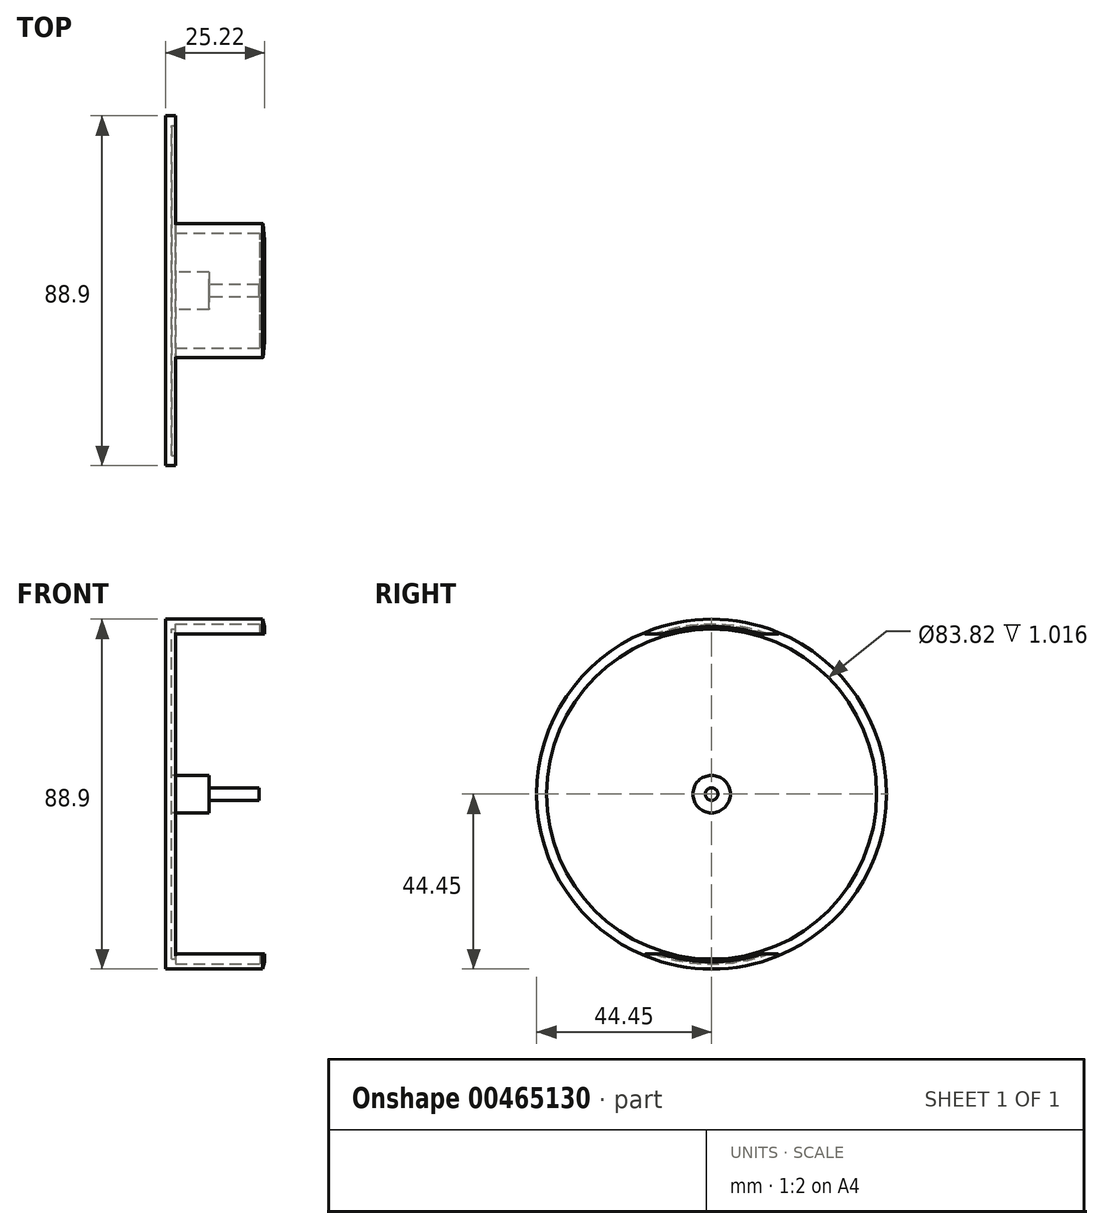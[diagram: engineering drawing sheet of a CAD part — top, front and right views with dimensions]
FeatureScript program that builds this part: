
annotation { "Feature Type Name" : "Feature", "Feature Type Description" : "" }
export const myFeature = defineFeature(function(context is Context, id is Id, definition is map)
    precondition{}
    {
        {
            var Q0;
            Q0=qCreatedBy(makeId("Right.planeOp"),FACE);
            var sketch = newSketch(context, id + "F0", { "sketchPlane" : qUnion([Q0])});
            skCircle(sketch, "E0", {"center": v(0, 0) * mm, "radius": 44.45 * mm});
            skSolve(sketch);
        }
        {
            var Q0;
            Q0 = qSketchRegion(id + "F0", true);
            extrude(context, id + "F1", {"entities" : qUnion([Q0]), "depth" : 25.4 * mm});
        }
        {
            var Q0;
            Q0=makeQuery(id+"F1.opExtrude","CAP_FACE",FACE,{"disambiguationData":[OSD([sQuery(id+"F0.wireOp",EDGE,"E0")])],"isStart":false});
            var sketch = newSketch(context, id + "F2", { "sketchPlane" : qUnion([Q0])});
            skCircle(sketch, "E1", {"center": v(0, 0) * mm, "radius": 43.18 * mm});
            skSolve(sketch);
        }
        {
            var Q0;
            Q0 = qSketchRegion(id + "F2", true);
            extrude(context, id + "F3", {"entities" : qUnion([Q0]), "operationType" : NewBodyOperationType.REMOVE, "oppositeDirection" : true, "depth" : 22.86 * mm});
        }
        {
            var Q0;
            Q0=makeQuery(id+"F1.opExtrude","CAP_FACE",FACE,{"disambiguationData":[OSD([sQuery(id+"F0.wireOp",EDGE,"E0")])],"isStart":false});
            var sketch = newSketch(context, id + "F4", { "sketchPlane" : qUnion([Q0])});
            skCircle(sketch, "E2", {"center": v(0, 0) * mm, "radius": 44.45 * mm});
            skCircle(sketch, "E3", {"center": v(0, 0) * mm, "radius": 42.55 * mm});
            skSolve(sketch);
        }
        {
            var Q0;
            Q0 = qSketchRegion(id + "F4", true);
            extrude(context, id + "F5", {"entities" : qUnion([Q0]), "operationType" : NewBodyOperationType.ADD, "oppositeDirection" : true, "depth" : 1.27 * mm});
        }
        {
            var Q0;
            Q0=qCreatedBy(makeId("Front.planeOp"),FACE);
            var sketch = newSketch(context, id + "F6", { "sketchPlane" : qUnion([Q0])});
            skLineSegment(sketch, "E4.bottom", {"start": v(27.94, 40.64) * mm, "end": v(2.54, 40.64) * mm});
            skLineSegment(sketch, "E4.top", {"start": v(27.94, -40.64) * mm, "end": v(2.54, -40.64) * mm});
            skLineSegment(sketch, "E4.left", {"start": v(27.94, 40.64) * mm, "end": v(27.94, -40.64) * mm});
            skLineSegment(sketch, "E4.right", {"start": v(2.54, 40.64) * mm, "end": v(2.54, -40.64) * mm});
            skLineSegment(sketch, "E5", {"start": v(0, 0) * mm, "end": v(2.54, 0) * mm, "construction": true});
            skSolve(sketch);
        }
        {
            var Q0;
            Q0 = qSketchRegion(id + "F6", true);
            extrude(context, id + "F7", {"entities" : qUnion([Q0]), "operationType" : NewBodyOperationType.REMOVE, "oppositeDirection" : true, "depth" : 127 * mm, "symmetric" : true});
        }
        {
            var Q0;
            {var subQ0=sQuery(id+"F4.wireOp",EDGE,"E3");Q0=makeQuery(id+"F7.boolean.opBoolean","SPLIT",EDGE,{"disambiguationData":[TD([makeQuery(id+"F7.opExtrude","SWEPT_FACE",FACE,{"disambiguationData":[OSD([sQuery(id+"F6.wireOp",EDGE,"E4.top")])]})])],"derivedFrom":makeQuery(id+"F5.opExtrude","CAP_EDGE",EDGE,{"disambiguationData":[OSD([subQ0])],"isStart":false})});}
            var Q1;
            {var subQ0=sQuery(id+"F4.wireOp",EDGE,"E3");Q1=makeQuery(id+"F7.boolean.opBoolean","SPLIT",EDGE,{"disambiguationData":[TD([makeQuery(id+"F7.opExtrude","SWEPT_FACE",FACE,{"disambiguationData":[OSD([sQuery(id+"F6.wireOp",EDGE,"E4.bottom")])]})])],"derivedFrom":makeQuery(id+"F5.opExtrude","CAP_EDGE",EDGE,{"disambiguationData":[OSD([subQ0])],"isStart":false})});}
            chamfer(context, id + "F8", {"entities" : qUnion([Q0, Q1]), "chamferType" : ChamferType.OFFSET_ANGLE, "width" : 1.27 * mm, "oppositeDirection" : true, "angle" : 15 * degree, "tangentPropagation" : true});
        }
        {
            var Q0;
            {var subQ0=sQuery(id+"F0.wireOp",EDGE,"E0");Q0=makeQuery(id+"F7.boolean.opBoolean","SPLIT",EDGE,{"disambiguationData":[TD([makeQuery(id+"F7.opExtrude","SWEPT_FACE",FACE,{"disambiguationData":[OSD([sQuery(id+"F6.wireOp",EDGE,"E4.top")])]})])],"derivedFrom":makeQuery(id+"F1.opExtrude","CAP_EDGE",EDGE,{"disambiguationData":[OSD([subQ0])],"isStart":false})});}
            var Q1;
            {var subQ0=sQuery(id+"F0.wireOp",EDGE,"E0");Q1=makeQuery(id+"F7.boolean.opBoolean","SPLIT",EDGE,{"disambiguationData":[TD([makeQuery(id+"F7.opExtrude","SWEPT_FACE",FACE,{"disambiguationData":[OSD([sQuery(id+"F6.wireOp",EDGE,"E4.bottom")])]})])],"derivedFrom":makeQuery(id+"F1.opExtrude","CAP_EDGE",EDGE,{"disambiguationData":[OSD([subQ0])],"isStart":false})});}
            chamfer(context, id + "F9", {"entities" : qUnion([Q0, Q1]), "chamferType" : ChamferType.OFFSET_ANGLE, "width" : 2.54 * mm, "oppositeDirection" : true, "angle" : 15 * degree, "tangentPropagation" : true});
        }
        {
            var Q0;
            Q0=makeQuery(id+"F7.boolean.opBoolean","INTERSECT",EDGE,{"disambiguationData":[OD(0.0)],"derivedFrom":[makeQuery(id+"F1.opExtrude","SWEPT_FACE",FACE,{"disambiguationData":[OSD([sQuery(id+"F0.wireOp",EDGE,"E0")])]}),makeQuery(id+"F7.opExtrude","SWEPT_FACE",FACE,{"disambiguationData":[OSD([sQuery(id+"F6.wireOp",EDGE,"E4.top")])]})]});
            var Q1;
            Q1=makeQuery(id+"F7.boolean.opBoolean","INTERSECT",EDGE,{"disambiguationData":[OD(1.0)],"derivedFrom":[makeQuery(id+"F1.opExtrude","SWEPT_FACE",FACE,{"disambiguationData":[OSD([sQuery(id+"F0.wireOp",EDGE,"E0")])]}),makeQuery(id+"F7.opExtrude","SWEPT_FACE",FACE,{"disambiguationData":[OSD([sQuery(id+"F6.wireOp",EDGE,"E4.top")])]})]});
            var Q2;
            Q2=makeQuery(id+"F7.boolean.opBoolean","INTERSECT",EDGE,{"disambiguationData":[OD(0.0)],"derivedFrom":[makeQuery(id+"F1.opExtrude","SWEPT_FACE",FACE,{"disambiguationData":[OSD([sQuery(id+"F0.wireOp",EDGE,"E0")])]}),makeQuery(id+"F7.opExtrude","SWEPT_FACE",FACE,{"disambiguationData":[OSD([sQuery(id+"F6.wireOp",EDGE,"E4.bottom")])]})]});
            var Q3;
            Q3=makeQuery(id+"F7.boolean.opBoolean","INTERSECT",EDGE,{"disambiguationData":[OD(1.0)],"derivedFrom":[makeQuery(id+"F1.opExtrude","SWEPT_FACE",FACE,{"disambiguationData":[OSD([sQuery(id+"F0.wireOp",EDGE,"E0")])]}),makeQuery(id+"F7.opExtrude","SWEPT_FACE",FACE,{"disambiguationData":[OSD([sQuery(id+"F6.wireOp",EDGE,"E4.bottom")])]})]});
            fillet(context, id + "F10", {"entities" : qUnion([Q0, Q1, Q2, Q3]), "radius" : 0.25 * mm, "tangentPropagation" : true, "allowEdgeOverflow" : false});
        }
        {
            var Q0;
            Q0=makeQuery(id+"F7.boolean.opBoolean","MERGE",FACE,{"derivedFrom":[makeQuery(id+"F3.boolean.opBoolean","COPY",FACE,{"derivedFrom":makeQuery(id+"F3.opExtrude","CAP_FACE",FACE,{"disambiguationData":[OSD([sQuery(id+"F2.wireOp",EDGE,"E1")])],"isStart":false})}),makeQuery(id+"F7.opExtrude","SWEPT_FACE",FACE,{"disambiguationData":[OSD([sQuery(id+"F6.wireOp",EDGE,"E4.right")])]})]});
            var sketch = newSketch(context, id + "F11", { "sketchPlane" : qUnion([Q0])});
            skCircle(sketch, "E6", {"center": v(0, 0) * mm, "radius": 41.91 * mm});
            skSolve(sketch);
        }
        {
            var Q0;
            Q0 = qSketchRegion(id + "F11", true);
            extrude(context, id + "F12", {"entities" : qUnion([Q0]), "operationType" : NewBodyOperationType.REMOVE, "oppositeDirection" : true, "depth" : 1.02 * mm});
        }
        {
            var Q0;
            Q0=makeQuery(id+"F12.boolean.opBoolean","COPY",FACE,{"derivedFrom":makeQuery(id+"F12.opExtrude","CAP_FACE",FACE,{"disambiguationData":[OSD([sQuery(id+"F11.wireOp",EDGE,"E6")])],"isStart":false})});
            var sketch = newSketch(context, id + "F13", { "sketchPlane" : qUnion([Q0])});
            skCircle(sketch, "E7", {"center": v(0, 0) * mm, "radius": 4.76 * mm});
            skSolve(sketch);
        }
        {
            var Q0;
            Q0 = qSketchRegion(id + "F13", true);
            extrude(context, id + "F14", {"entities" : qUnion([Q0]), "operationType" : NewBodyOperationType.ADD, "depth" : 9.52 * mm});
        }
        {
            var Q0;
            Q0=makeQuery(id+"F14.opExtrude","CAP_FACE",FACE,{"disambiguationData":[OSD([sQuery(id+"F13.wireOp",EDGE,"E7")])],"isStart":false});
            var sketch = newSketch(context, id + "F15", { "sketchPlane" : qUnion([Q0])});
            skCircle(sketch, "E8", {"center": v(0, 0) * mm, "radius": 1.59 * mm});
            skSolve(sketch);
        }
        {
            var Q0;
            Q0 = qSketchRegion(id + "F15", true);
            extrude(context, id + "F16", {"entities" : qUnion([Q0]), "operationType" : NewBodyOperationType.ADD, "depth" : 12.7 * mm});
        }
    });
